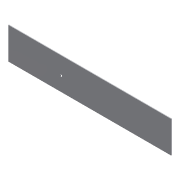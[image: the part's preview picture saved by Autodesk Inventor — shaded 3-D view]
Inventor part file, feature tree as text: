
AUTODESK INVENTOR PART (.ipt)
format: ipt  version: 2016 (Build 200138000, 138)  size: 113,664 bytes
history: native  units: mm
features: hole x2, extrude x1, sketch x1
ambient origin geometry x8: Origin, YZ Plane, XZ Plane, XY Plane, X Axis, Y Axis, Z Axis, Center Point
bodies: Solid1 (feature_tree)
feature tree (4):
  extrude  "Extrusion1"  Depth=2.0mm
  hole  "Hole1"  [1 undecoded]
  hole  "Hole2"  [1 undecoded]
  sketch  "Sketch1"  dims[d0=462.0mm d1=2.0mm d2=90.0mm d3=0.0mm d4=150.0mm d5=50.0mm d6=6.0mm d7=6.0mm d8=4.0mm d9=2.0mm d10=90.0deg d11=8.0mm d12=20.594885mm d13=400.0mm d14=50.0mm d15=6.0mm d16=6.0mm d17=4.0mm d18=2.0mm d19=90.0deg d20=8.0mm d21=20.594885mm]
note: 2 required parameter values undecoded (feature->parameter linkage not recoverable at this tier; creation-order binding heuristic only, values carry confidence <= 0.55)
